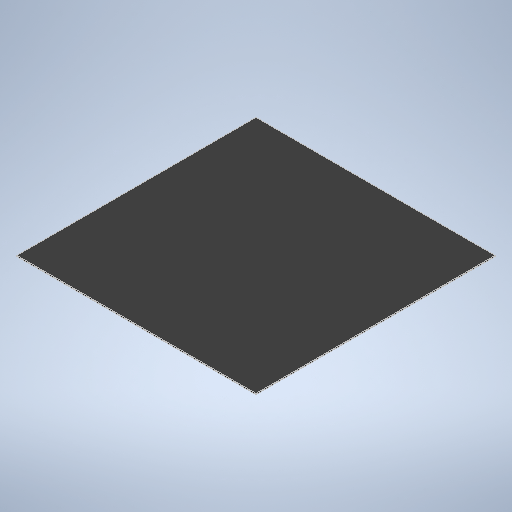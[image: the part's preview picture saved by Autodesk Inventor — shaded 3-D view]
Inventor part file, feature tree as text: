
AUTODESK INVENTOR PART (.ipt)
format: ipt  version: 2025 (Build 290162010, 162A)  size: 213,504 bytes
history: native  units: in
note: dims shown in document units (in); Inventor stores cm internally (conversion verified against a paired STEP export)
features: extrude x1, sketch x1
ambient origin geometry x8: Origin, YZ Plane, XZ Plane, XY Plane, X Axis, Y Axis, Z Axis, Center Point
bodies: Solid1 (feature_tree)
feature tree (2):
  extrude  "Extrusion1"  Depth=0.0625in TaperAngle=0.0deg
  sketch  "Sketch1"  dims[d1=14.0in d2=0.0625in d3=0.0in]
